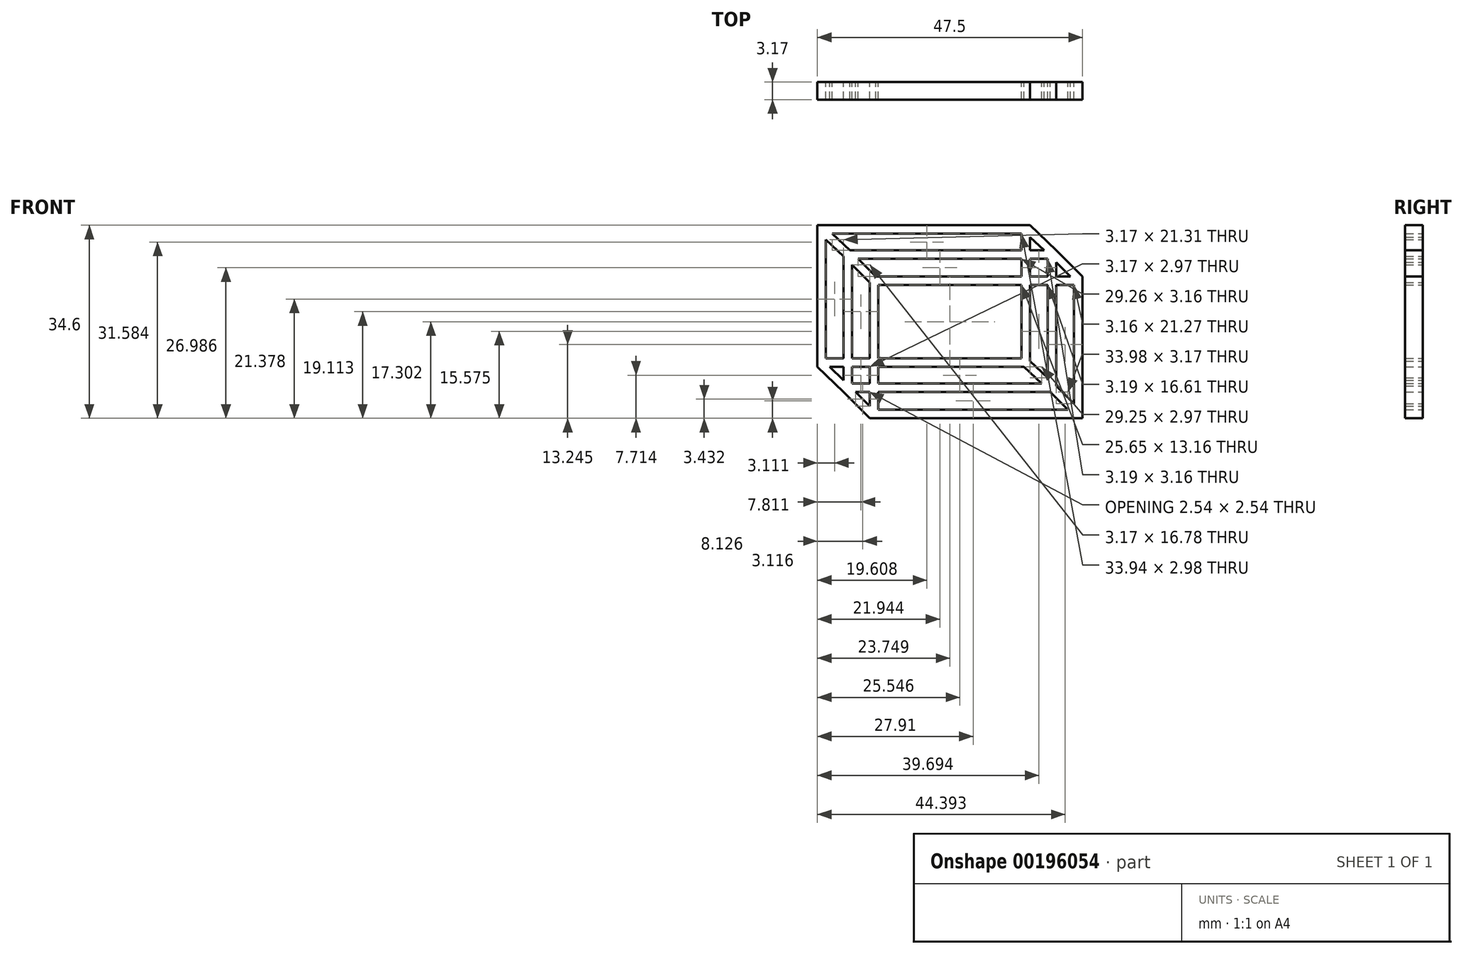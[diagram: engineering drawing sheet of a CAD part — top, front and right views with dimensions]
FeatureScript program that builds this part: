
annotation { "Feature Type Name" : "Feature", "Feature Type Description" : "" }
export const myFeature = defineFeature(function(context is Context, id is Id, definition is map)
    precondition{}
    {
        {
            var Q0;
            Q0=qCreatedBy(makeId("Front.planeOp"),FACE);
            var sketch = newSketch(context, id + "F0", { "sketchPlane" : qUnion([Q0])});
            skLineSegment(sketch, "E0.bottom", {"start": v(0, 0) * mm, "end": v(38.1, 0) * mm});
            skLineSegment(sketch, "E0.top", {"start": v(2.2, -25.4) * mm, "end": v(4.7, -25.4) * mm});
            skLineSegment(sketch, "E0.left", {"start": v(0, 0) * mm, "end": v(0, -25.4) * mm});
            skLineSegment(sketch, "E0.right", {"start": v(38.1, -2.1) * mm, "end": v(38.1, -4.5) * mm});
            skLineSegment(sketch, "E1.0", {"start": v(2.64, -1.52) * mm, "end": v(36.58, -1.52) * mm});
            skLineSegment(sketch, "E1.1", {"start": v(1.52, -2.57) * mm, "end": v(1.52, -23.88) * mm});
            skLineSegment(sketch, "E1.2", {"start": v(1.52, -23.88) * mm, "end": v(4.7, -23.88) * mm});
            skLineSegment(sketch, "E1.3", {"start": v(36.58, -1.52) * mm, "end": v(36.58, -4.5) * mm});
            skPoint(sketch, "E2", {"position": v(4.7, -4.5) * mm});
            skLineSegment(sketch, "E3.bottom", {"start": v(5.83, -4.5) * mm, "end": v(36.58, -4.5) * mm});
            skLineSegment(sketch, "E3.top", {"start": v(6.85, -29.9) * mm, "end": v(9.4, -29.9) * mm});
            skLineSegment(sketch, "E3.left", {"start": v(4.7, -5.54) * mm, "end": v(4.7, -23.88) * mm});
            skLineSegment(sketch, "E3.right", {"start": v(42.81, -6.66) * mm, "end": v(42.81, -9.2) * mm});
            skLineSegment(sketch, "E4.0", {"start": v(7.31, -6.03) * mm, "end": v(36.58, -6.03) * mm});
            skLineSegment(sketch, "E4.1", {"start": v(6.22, -7.1) * mm, "end": v(6.22, -23.88) * mm});
            skLineSegment(sketch, "E4.2", {"start": v(6.22, -28.37) * mm, "end": v(9.4, -28.37) * mm});
            skLineSegment(sketch, "E4.3", {"start": v(41.29, -6.03) * mm, "end": v(41.29, -9.2) * mm});
            skPoint(sketch, "E5", {"position": v(9.4, -9.2) * mm});
            skLineSegment(sketch, "E6.bottom", {"start": v(10.48, -9.2) * mm, "end": v(36.58, -9.2) * mm});
            skLineSegment(sketch, "E6.left", {"start": v(9.4, -10.27) * mm, "end": v(9.4, -23.88) * mm});
            skLineSegment(sketch, "E6.right", {"start": v(47.5, -9.2) * mm, "end": v(47.5, -34.6) * mm});
            skLineSegment(sketch, "E7.0", {"start": v(9.4, -34.6) * mm, "end": v(47.5, -34.6) * mm});
            skLineSegment(sketch, "E8.0", {"start": v(10.92, -10.72) * mm, "end": v(36.58, -10.72) * mm});
            skLineSegment(sketch, "E8.1", {"start": v(10.92, -10.72) * mm, "end": v(10.92, -23.88) * mm});
            skLineSegment(sketch, "E8.2", {"start": v(10.92, -33.07) * mm, "end": v(44.9, -33.07) * mm});
            skLineSegment(sketch, "E8.3", {"start": v(45.97, -10.72) * mm, "end": v(45.97, -32) * mm});
            skLineSegment(sketch, "E9.0", {"start": v(1.52, -2.57) * mm, "end": v(4.7, -5.54) * mm});
            skLineSegment(sketch, "E10.0", {"start": v(2.64, -1.52) * mm, "end": v(5.83, -4.5) * mm});
            skLineSegment(sketch, "E11.0", {"start": v(6.22, -7.1) * mm, "end": v(9.4, -10.27) * mm});
            skLineSegment(sketch, "E12.0", {"start": v(7.31, -6.03) * mm, "end": v(10.48, -9.2) * mm});
            skLineSegment(sketch, "E13", {"start": v(0, -25.4) * mm, "end": v(4.7, -29.9) * mm});
            skLineSegment(sketch, "E14.0", {"start": v(2.2, -25.4) * mm, "end": v(4.7, -27.79) * mm});
            skLineSegment(sketch, "E15", {"start": v(4.7, -29.9) * mm, "end": v(9.4, -34.6) * mm});
            skLineSegment(sketch, "E16.0", {"start": v(6.85, -29.9) * mm, "end": v(9.4, -32.44) * mm});
            skLineSegment(sketch, "E17.trimOffspring", {"start": v(6.22, -23.88) * mm, "end": v(9.4, -23.88) * mm});
            skLineSegment(sketch, "E18.trimOffspring", {"start": v(6.22, -25.4) * mm, "end": v(9.4, -25.4) * mm});
            skLineSegment(sketch, "E19.trimOffspring", {"start": v(6.22, -25.4) * mm, "end": v(6.22, -28.37) * mm});
            skLineSegment(sketch, "E20.trimOffspring", {"start": v(4.7, -25.4) * mm, "end": v(4.7, -27.79) * mm});
            skLineSegment(sketch, "E21.trimOffspring", {"start": v(10.92, -23.88) * mm, "end": v(36.58, -23.88) * mm});
            skLineSegment(sketch, "E22.trimOffspring", {"start": v(9.4, -25.4) * mm, "end": v(9.4, -28.37) * mm});
            skLineSegment(sketch, "E23.trimOffspring", {"start": v(10.92, -25.4) * mm, "end": v(10.92, -28.37) * mm});
            skLineSegment(sketch, "E24.trimOffspring", {"start": v(10.92, -25.4) * mm, "end": v(36.98, -25.4) * mm});
            skLineSegment(sketch, "E25.trimOffspring", {"start": v(9.4, -29.9) * mm, "end": v(9.4, -32.44) * mm});
            skLineSegment(sketch, "E26.trimOffspring", {"start": v(10.92, -29.9) * mm, "end": v(10.92, -33.07) * mm});
            skLineSegment(sketch, "E27.trimOffspring", {"start": v(10.92, -28.37) * mm, "end": v(40.17, -28.37) * mm});
            skLineSegment(sketch, "E28.trimOffspring", {"start": v(10.92, -29.9) * mm, "end": v(41.74, -29.9) * mm});
            skLineSegment(sketch, "E29.trimOffspring", {"start": v(38.1, -4.5) * mm, "end": v(40.6, -4.5) * mm});
            skLineSegment(sketch, "E30.trimOffspring", {"start": v(38.1, -6.03) * mm, "end": v(38.1, -9.2) * mm});
            skLineSegment(sketch, "E31.trimOffspring", {"start": v(38.1, -6.03) * mm, "end": v(41.29, -6.03) * mm});
            skLineSegment(sketch, "E32.trimOffspring", {"start": v(36.58, -6.03) * mm, "end": v(36.58, -9.2) * mm});
            skLineSegment(sketch, "E33.trimOffspring", {"start": v(38.1, -9.2) * mm, "end": v(41.29, -9.2) * mm});
            skLineSegment(sketch, "E34.trimOffspring", {"start": v(38.1, -10.72) * mm, "end": v(38.1, -24.36) * mm});
            skLineSegment(sketch, "E35.trimOffspring", {"start": v(36.58, -10.72) * mm, "end": v(36.58, -23.88) * mm});
            skLineSegment(sketch, "E36.trimOffspring", {"start": v(38.1, -10.72) * mm, "end": v(41.29, -10.72) * mm});
            skLineSegment(sketch, "E37.trimOffspring", {"start": v(41.29, -10.72) * mm, "end": v(41.29, -27.33) * mm});
            skLineSegment(sketch, "E38.trimOffspring", {"start": v(42.81, -10.72) * mm, "end": v(42.81, -28.82) * mm});
            skLineSegment(sketch, "E39.trimOffspring", {"start": v(42.81, -9.2) * mm, "end": v(45.34, -9.2) * mm});
            skLineSegment(sketch, "E40.trimOffspring", {"start": v(42.81, -10.72) * mm, "end": v(45.97, -10.72) * mm});
            skLineSegment(sketch, "E41", {"start": v(38.1, 0) * mm, "end": v(42.81, -4.5) * mm});
            skLineSegment(sketch, "E42", {"start": v(42.81, -4.5) * mm, "end": v(47.5, -9.2) * mm});
            skLineSegment(sketch, "E43.0", {"start": v(38.1, -2.1) * mm, "end": v(40.6, -4.5) * mm});
            skLineSegment(sketch, "E44.trimOffspring", {"start": v(42.81, -6.66) * mm, "end": v(45.34, -9.2) * mm});
            skLineSegment(sketch, "E45.0", {"start": v(36.98, -25.4) * mm, "end": v(40.17, -28.37) * mm});
            skLineSegment(sketch, "E46.0", {"start": v(38.1, -24.36) * mm, "end": v(41.29, -27.33) * mm});
            skLineSegment(sketch, "E47.0", {"start": v(41.74, -29.9) * mm, "end": v(44.9, -33.07) * mm});
            skLineSegment(sketch, "E48.0", {"start": v(42.81, -28.82) * mm, "end": v(45.97, -32) * mm});
            skSolve(sketch);
        }
        {
            var Q0;
            Q0=makeQuery(id+"F0.imprint","IMPRINT",FACE,{"disambiguationData":[TD([[makeQuery(id+"F0.imprint","IMPRINT",EDGE,{"derivedFrom":sQuery(id+"F0.wireOp",EDGE,"E0.bottom")}),-1.0]])]});
            extrude(context, id + "F1", {"entities" : qUnion([Q0]), "depth" : 3.17 * mm, "offsetDistance" : 25.4 * mm});
        }
    });
